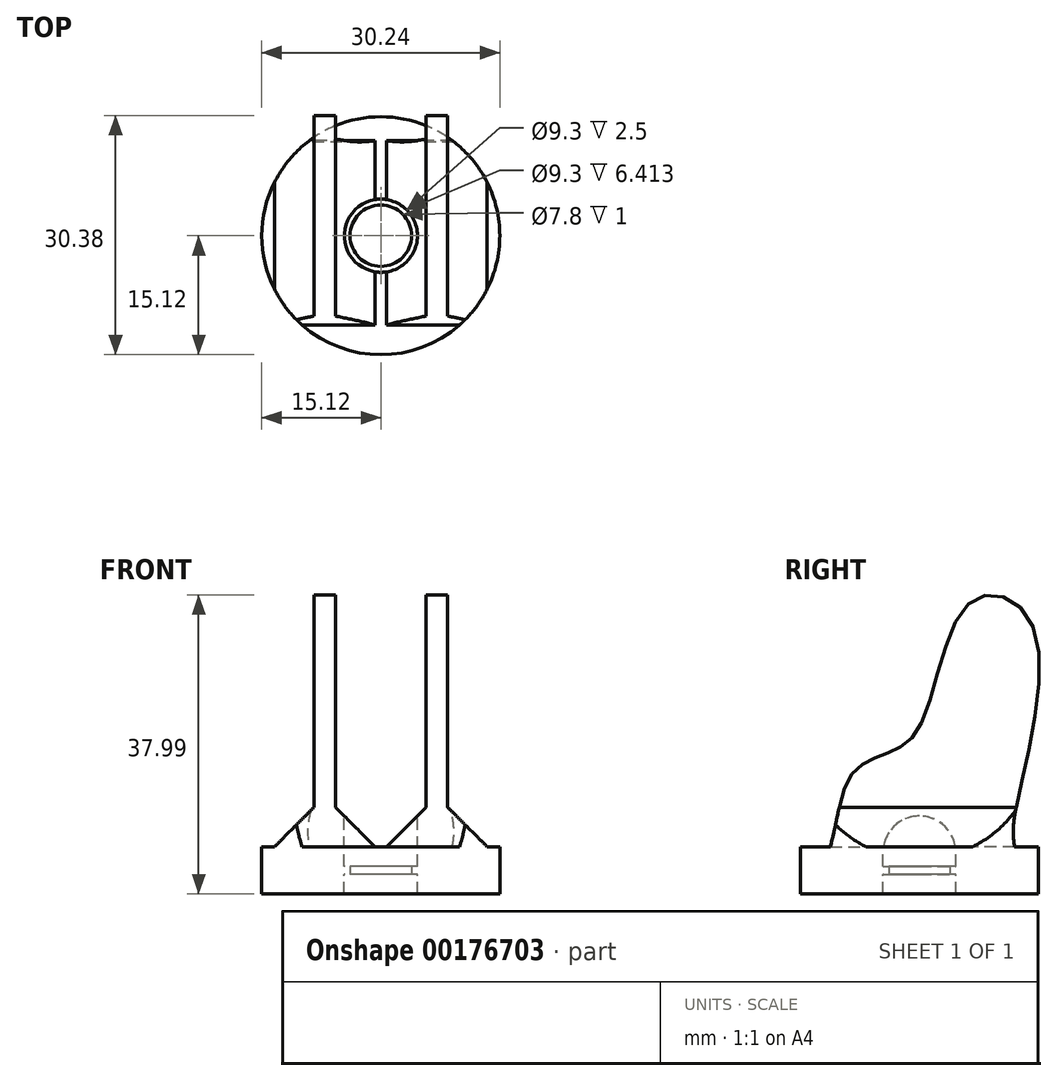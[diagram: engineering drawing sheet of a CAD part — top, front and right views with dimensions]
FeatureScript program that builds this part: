
annotation { "Feature Type Name" : "Feature", "Feature Type Description" : "" }
export const myFeature = defineFeature(function(context is Context, id is Id, definition is map)
    precondition{}
    {
        {
            var Q0;
            Q0=qCreatedBy(makeId("Right.planeOp"),FACE);
            var sketch = newSketch(context, id + "F0", { "sketchPlane" : qUnion([Q0])});
            skFitSpline(sketch, "E0", {"points": [v(-12.5, 0) * mm, v(-9.03, 11.5) * mm, v(-4.66, 14.7) * mm, v(0, 18.18) * mm, v(6.62, 34.16) * mm, v(14.43, 31.01) * mm, v(12.09, 6.82) * mm, v(12.5, 0) * mm], "startDerivative": vector(39.23, 73.75) * mm, "endDerivative": vector(9.2, -85.4) * mm});
            skLineSegment(sketch, "E1", {"start": v(12.5, 0) * mm, "end": v(-12.5, 0) * mm});
            skSolve(sketch);
        }
        {
            var Q0;
            Q0=qSketchRegion(id+"F0",true);
            extrude(context, id + "F1", {"entities" : qUnion([Q0]), "endBound" : BoundingType.SYMMETRIC, "depth" : 17 * mm});
        }
        {
            var Q0;
            Q0=qSketchRegion(id+"F0",true);
            extrude(context, id + "F2", {"entities" : qUnion([Q0]), "operationType" : NewBodyOperationType.REMOVE, "endBound" : BoundingType.SYMMETRIC, "oppositeDirection" : true, "depth" : 11.5 * mm});
        }
        {
            var Q0;
            Q0=qCreatedBy(makeId("Top.planeOp"),FACE);
            var sketch = newSketch(context, id + "F3", { "sketchPlane" : qUnion([Q0])});
            skCircle(sketch, "E2", {"center": v(0, 0) * mm, "radius": 15.12 * mm});
            skCircle(sketch, "E3", {"center": v(0, 0) * mm, "radius": 4.65 * mm});
            skCircle(sketch, "E4", {"center": v(0, 0) * mm, "radius": 3.9 * mm});
            skSolve(sketch);
        }
        {
            var Q0;
            Q0=qSketchRegion(id+"F3",true);
            extrude(context, id + "F4", {"entities" : qUnion([Q0]), "operationType" : NewBodyOperationType.ADD, "endBound" : BoundingType.SYMMETRIC, "oppositeDirection" : true, "depth" : 6 * mm});
        }
        {
            var Q0;
            Q0=makeQuery(id+"F3.imprint","IMPRINT",FACE,{"disambiguationData":[TD([[makeQuery(id+"F3.imprint","IMPRINT",EDGE,{"derivedFrom":sQuery(id+"F3.wireOp",EDGE,"E3")}),1.0]])]});
            extrude(context, id + "F5", {"entities" : qUnion([Q0]), "operationType" : NewBodyOperationType.ADD, "endBound" : BoundingType.SYMMETRIC, "depth" : 1 * mm});
        }
        {
            var Q0;
            Q0=makeQuery(id+"F4.boolean.opBoolean","INTERSECT",EDGE,{"derivedFrom":[makeQuery(id+"F1.opExtrude","CAP_FACE",FACE,{"disambiguationData":[OSD([sQuery(id+"F0.wireOp",EDGE,"E0"),sQuery(id+"F0.wireOp",EDGE,"E1"),sQuery(id+"F0.wireOp",EDGE,"6enSXdvp-eGzs-tT8W-9ZCD-L5k8VryG9LG5")])],"isStart":false}),makeQuery(id+"F4.opExtrude","CAP_FACE",FACE,{"disambiguationData":[OSD([sQuery(id+"F3.wireOp",EDGE,"E2"),sQuery(id+"F3.wireOp",EDGE,"E3")])],"isStart":true})]});
            var Q1;
            Q1=makeQuery(id+"F4.boolean.opBoolean","INTERSECT",EDGE,{"derivedFrom":[makeQuery(id+"F2.boolean.opBoolean","COPY",FACE,{"derivedFrom":makeQuery(id+"F2.opExtrude","CAP_FACE",FACE,{"disambiguationData":[OSD([sQuery(id+"F0.wireOp",EDGE,"E0"),sQuery(id+"F0.wireOp",EDGE,"E1"),sQuery(id+"F0.wireOp",EDGE,"6enSXdvp-eGzs-tT8W-9ZCD-L5k8VryG9LG5")])],"isStart":true})}),makeQuery(id+"F4.opExtrude","CAP_FACE",FACE,{"disambiguationData":[OSD([sQuery(id+"F3.wireOp",EDGE,"E2"),sQuery(id+"F3.wireOp",EDGE,"E3")])],"isStart":true})]});
            var Q2;
            Q2=makeQuery(id+"F4.boolean.opBoolean","INTERSECT",EDGE,{"derivedFrom":[makeQuery(id+"F2.boolean.opBoolean","COPY",FACE,{"derivedFrom":makeQuery(id+"F2.opExtrude","CAP_FACE",FACE,{"disambiguationData":[OSD([sQuery(id+"F0.wireOp",EDGE,"E0"),sQuery(id+"F0.wireOp",EDGE,"E1"),sQuery(id+"F0.wireOp",EDGE,"6enSXdvp-eGzs-tT8W-9ZCD-L5k8VryG9LG5")])],"isStart":false})}),makeQuery(id+"F4.opExtrude","CAP_FACE",FACE,{"disambiguationData":[OSD([sQuery(id+"F3.wireOp",EDGE,"E2"),sQuery(id+"F3.wireOp",EDGE,"E3")])],"isStart":true})]});
            var Q3;
            Q3=makeQuery(id+"F4.boolean.opBoolean","INTERSECT",EDGE,{"derivedFrom":[makeQuery(id+"F1.opExtrude","CAP_FACE",FACE,{"disambiguationData":[OSD([sQuery(id+"F0.wireOp",EDGE,"E0"),sQuery(id+"F0.wireOp",EDGE,"E1"),sQuery(id+"F0.wireOp",EDGE,"6enSXdvp-eGzs-tT8W-9ZCD-L5k8VryG9LG5")])],"isStart":true}),makeQuery(id+"F4.opExtrude","CAP_FACE",FACE,{"disambiguationData":[OSD([sQuery(id+"F3.wireOp",EDGE,"E2"),sQuery(id+"F3.wireOp",EDGE,"E3")])],"isStart":true})]});
            chamfer(context, id + "F6", {"entities" : qUnion([Q0, Q1, Q2, Q3]), "width" : 5 * mm, "tangentPropagation" : true});
        }
    });
